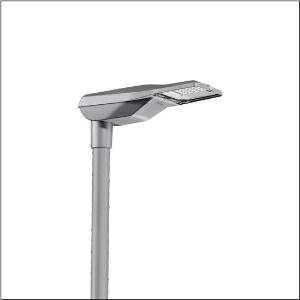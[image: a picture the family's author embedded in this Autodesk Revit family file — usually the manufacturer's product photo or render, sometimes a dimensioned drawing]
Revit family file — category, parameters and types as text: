
# Revit family: streetlight_sl_21_iq_micro___st1_0ab_5xe1m31d08cb_a4c0
name_source: partatom
category: Lighting Fixtures
units: mm (PartAtom-declared; Revit-internal decimal feet)

## family parameters
Cut with Voids When Loaded = No
Host = Face
Light Source = No
Part Type = Normal
Room Calculation Point = No
Round Connector Dimension = Use Diameter
Shared = No

## types (1)
- --- (1 x LED, 2520 lm, 19.4 W, 3000K)
    Apparent Load = 19 VA
    CIE Flux Codes = 38 73 97 100 100
    Color Rendering = 70
    Color Temperature = 3000K
    Default Elevation = 1800 mm
    Description = Streetlight SL 21 iQ micro, mast luminaire, primary light control with lens, of PMMA, primary optical cover: cover, of toughened safety glass, transparent, light distribution: ST1.0aB, light emission: direct distribution, primary light characteristic: asymmetric, installation type: post-top, side-entry, LED, High Power LED, rated luminous flux: 2.520lm, luminous efficacy: 130lm/W, light colour: 730, colour temperature: 3000K, control: Auto-Match, Temp-Guard, Lumen-Switch, Night-Set, Smart-Wire, Light-Fading, Desk-Remote (wireless, voltage-free reading and setting of iQ features in the workshop via application-optimized NFC function/RFID function), optimised constant luminous flux control (CLO 2.0), presetting dimming linear, mains connection: 220..240V, AC, 50/60Hz, start of lifetime: 19W, end of service life: 20W, reduction: 10W, luminaire housing, of diecast aluminium, powder-coated, Siteco® metallic grey (DB 702S), corrosivity category C5 mid according to DIN EN ISO 12944, please order mast flange separately, inclination adjustable: 0°, 5°, 10°, 15°, sealing non-destructively replaceable, multi-level sealing system, length: 528mm, width: 235mm, height: 110mm, mast flange for spigot size: 42mm (side-entry): 5XC10008XM4, 60/48mm (side-entry/post-top): 5XC10108XM2, 76/60mm (side-entry/post-top): 5XC10108XM1, protection rating (complete): IP66, insulation class (complete): insulation class II (safety insulation), certification: CE, ENEC, ENEC+, VDE, impact resistance: IK09, permissible operating ambient temperature for outdoor applications: -40..+50°C, standard-compliant lighting for roads and squares, packaging unit: 1 piece

Light Distribution: ST1.0aB
    Height = 110 mm
    Lamp = 1 x LED
    Lamp Light Flux = 2520 lm
    Lamp Power = 19.4 W
    Lamp count = 1
    Length = 528 mm
    Luminous efficacy = 130 lm/W
    Manufacturer = Siteco
    ModVariant = No
    Model = 5XE1M31D08CB
    Number of Poles = 1
    OnlyDefault = Yes
    Power Factor = 1
    Product Name = Streetlight SL 21 iQ micro | ST1.0aB
    Product group = mast luminaire | pylon top
    ProductGroupID = 6100
    Protection Class = Protection class II
    Protection Degree = IP 66
    RLX_Detail_Level = 1
    RLX_Emergency_Light_Flux = 0 lm
    RLX_Emergency_Type = 0
    RLX_Emergency_Type_DB = No
    RlxData = <blob elided: 98609 chars, md5=03201876>
    Socket = socket
    Standby Power = 0 W
    System Light Flux = 2520 lm
    System Power = 19 W
    Type Comments = factory setting: luminous flux: 100 % | dim-lin: 254 | 387 mA
    Type Image = l_1006881.jpg
    URL = http://relux.com
    VarID = @adj_069505
    Voltage = 0 V
    Weight = 0.00 kg
    Width = 235 mm

## geometry (parser evidence)
native form markers: Blend x4, Sweep x8
no freeform markers — native parametric forms only
